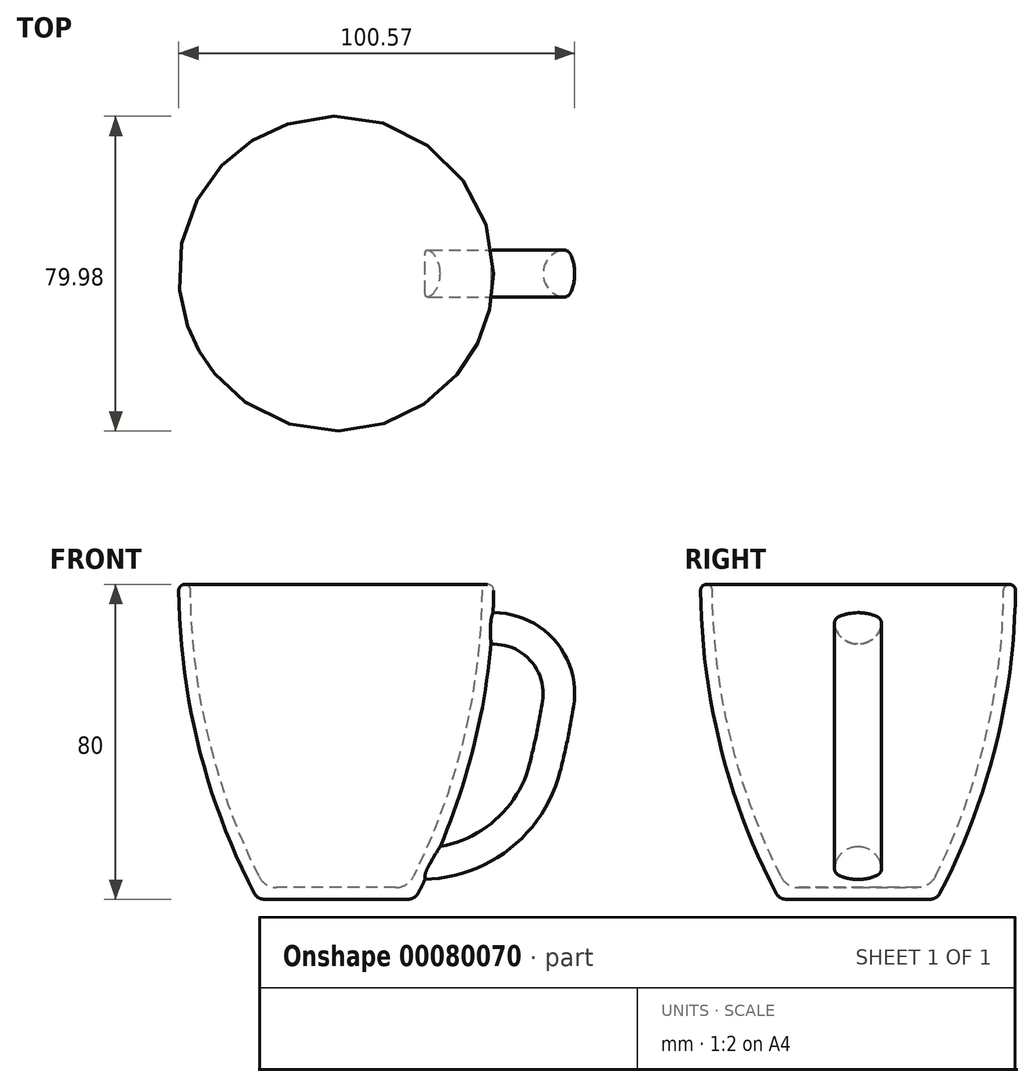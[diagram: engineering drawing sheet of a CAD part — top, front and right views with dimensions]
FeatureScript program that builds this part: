
annotation { "Feature Type Name" : "Feature", "Feature Type Description" : "" }
export const myFeature = defineFeature(function(context is Context, id is Id, definition is map)
    precondition{}
    {
        {
            var Q0;
            Q0=qCreatedBy(makeId("Front.planeOp"),FACE);
            var sketch = newSketch(context, id + "F0", { "sketchPlane" : qUnion([Q0])});
            skLineSegment(sketch, "E0", {"start": v(0, 3) * mm, "end": v(0, 0) * mm});
            skLineSegment(sketch, "E1", {"start": v(0, 0) * mm, "end": v(20, 0) * mm});
            skArc(sketch, "E2", {"start": v(20, 0) * mm, "mid": v(34.92, 38.77) * mm, "end": v(40, 80) * mm});
            skArc(sketch, "E3.0", {"start": v(18.19, 3) * mm, "mid": v(32.23, 40.37) * mm, "end": v(37, 80) * mm});
            skLineSegment(sketch, "E3.1", {"start": v(0, 3) * mm, "end": v(18.19, 3) * mm});
            skLineSegment(sketch, "E4", {"start": v(37, 80) * mm, "end": v(40, 80) * mm});
            skLineSegment(sketch, "E5", {"start": v(40, 160) * mm, "end": v(40, 0) * mm, "construction": true});
            skLineSegment(sketch, "E6", {"start": v(37, 160) * mm, "end": v(37, 0) * mm, "construction": true});
            skSolve(sketch);
        }
        {
            var Q0;
            Q0=qSketchRegion(id+"F0",true);
            var Q1;
            Q1=sQuery(id+"F0.wireOp",EDGE,"E0");
            revolve(context, id + "F1", {"entities" : qUnion([Q0]), "axis" : qUnion([Q1]), "revolveType" : RevolveType.FULL});
        }
        {
            var Q0;
            Q0=sQuery(id+"F0.wireOp",EDGE,"E5");
            cPlane(context, id + "F2", {"entities" : qUnion([Q0]), "cplaneType" : CPlaneType.LINE_ANGLE, "offset" : 150 * mm, "angle" : 0 * degree, "width" : 150 * mm, "height" : 150 * mm});
        }
        {
            var Q0;
            Q0=qCreatedBy(id+"F2.planeOp",FACE);
            var sketch = newSketch(context, id + "F3", { "sketchPlane" : qUnion([Q0])});
            skPoint(sketch, "E7", {"position": v(0, 70) * mm});
            skArc(sketch, "E8", {"start": v(4.8, 71.83) * mm, "mid": v(0, 72.83) * mm, "end": v(-4.8, 71.83) * mm});
            skArc(sketch, "E9", {"start": v(4.8, 71.83) * mm, "mid": v(5.79, 70.9) * mm, "end": v(5.95, 69.54) * mm});
            skArc(sketch, "E10", {"start": v(-4.8, 71.83) * mm, "mid": v(-5.79, 70.9) * mm, "end": v(-5.95, 69.54) * mm});
            skArc(sketch, "E11", {"start": v(-5.95, 69.54) * mm, "mid": v(0, 64.83) * mm, "end": v(5.95, 69.54) * mm});
            skSolve(sketch);
        }
        {
            var Q0;
            Q0=qSketchRegion(id+"F3",true);
            extrude(context, id + "F4", {"entities" : qUnion([Q0]), "operationType" : NewBodyOperationType.ADD, "endBound" : BoundingType.UP_TO_NEXT, "depth" : 25 * mm});
        }
        {
            var Q0;
            Q0=qCreatedBy(makeId("Front.planeOp"),FACE);
            var sketch = newSketch(context, id + "F5", { "sketchPlane" : qUnion([Q0])});
            skArc(sketch, "E12", {"start": v(57.52, 49.4) * mm, "mid": v(53.52, 63.75) * mm, "end": v(40, 70) * mm});
            skLineSegment(sketch, "E13", {"start": v(42.52, 70) * mm, "end": v(37.48, 70) * mm, "construction": true});
            skArc(sketch, "E14", {"start": v(54.14, 33.16) * mm, "mid": v(56, 41.24) * mm, "end": v(57.52, 49.4) * mm});
            skArc(sketch, "E15", {"start": v(54.14, 33.16) * mm, "mid": v(43.14, 15.7) * mm, "end": v(24, 8) * mm});
            skLineSegment(sketch, "E16", {"start": v(-130, 80) * mm, "end": v(57.52, 49.4) * mm, "construction": true});
            skLineSegment(sketch, "E17", {"start": v(-130, 80) * mm, "end": v(54.14, 33.16) * mm, "construction": true});
            skSolve(sketch);
        }
        {
            var Q0;
            Q0=makeQuery(id+"F3.imprint","IMPRINT",FACE,{"disambiguationData":[TD([[makeQuery(id+"F3.imprint","IMPRINT",EDGE,{"derivedFrom":sQuery(id+"F3.wireOp",EDGE,"E8")}),1.0]])]});
            var Q1;
            Q1=sQuery(id+"F5.wireOp",EDGE,"E12");
            var Q2;
            Q2=sQuery(id+"F5.wireOp",EDGE,"E14");
            var Q3;
            Q3=sQuery(id+"F5.wireOp",EDGE,"E15");
            sweep(context, id + "F6", {"operationType" : NewBodyOperationType.ADD, "profiles" : qUnion([Q0]), "path" : qUnion([Q1, Q2, Q3])});
        }
        {
            var Q0;
            Q0=makeQuery(id+"F1.opRevolve","SWEPT_EDGE",EDGE,{"disambiguationData":[OSD([sQuery(id+"F0.wireOp",EDGE,"E3.0"),sQuery(id+"F0.wireOp",EDGE,"E4")])]});
            var Q1;
            Q1=makeQuery(id+"F1.opRevolve","SWEPT_EDGE",EDGE,{"disambiguationData":[OSD([sQuery(id+"F0.wireOp",EDGE,"E2"),sQuery(id+"F0.wireOp",EDGE,"E4")])]});
            fillet(context, id + "F7", {"entities" : qUnion([Q0, Q1]), "radius" : 1.5 * mm, "tangentPropagation" : true, "allowEdgeOverflow" : false});
        }
        {
            var Q0;
            Q0=makeQuery(id+"F1.opRevolve","SWEPT_EDGE",EDGE,{"disambiguationData":[OSD([sQuery(id+"F0.wireOp",EDGE,"E1"),sQuery(id+"F0.wireOp",EDGE,"E2")])]});
            fillet(context, id + "F8", {"entities" : qUnion([Q0]), "radius" : 3 * mm, "tangentPropagation" : true, "allowEdgeOverflow" : false});
        }
        {
            var Q0;
            Q0=makeQuery(id+"F1.opRevolve","SWEPT_EDGE",EDGE,{"disambiguationData":[OSD([sQuery(id+"F0.wireOp",EDGE,"E3.0"),sQuery(id+"F0.wireOp",EDGE,"E3.1")])]});
            fillet(context, id + "F9", {"entities" : qUnion([Q0]), "radius" : 5 * mm, "tangentPropagation" : true, "allowEdgeOverflow" : false});
        }
        {
            var Q0;
            Q0=makeQuery(id+"F6.opSweep","CAP_FACE",FACE,{"disambiguationData":[OSD([sQuery(id+"F3.wireOp",EDGE,"E8"),sQuery(id+"F3.wireOp",EDGE,"E9"),sQuery(id+"F3.wireOp",EDGE,"E10"),sQuery(id+"F3.wireOp",EDGE,"E11"),sQuery(id+"F5.wireOp",VERTEX,"E15.end")])],"isStart":false});
            var sketch = newSketch(context, id + "F10", { "sketchPlane" : qUnion([Q0])});
            skArc(sketch, "E18", {"start": v(5.95, 6.77) * mm, "mid": v(5.84, 7.17) * mm, "end": v(5.7, 7.57) * mm});
            skArc(sketch, "E19", {"start": v(4.8, 4.48) * mm, "mid": v(5.79, 5.41) * mm, "end": v(5.95, 6.77) * mm});
            skArc(sketch, "E20", {"start": v(-4.8, 4.48) * mm, "mid": v(0, 3.47) * mm, "end": v(4.8, 4.48) * mm});
            skArc(sketch, "E21", {"start": v(-5.95, 6.77) * mm, "mid": v(-5.79, 5.41) * mm, "end": v(-4.8, 4.48) * mm});
            skArc(sketch, "E22", {"start": v(-5.7, 7.57) * mm, "mid": v(-5.84, 7.17) * mm, "end": v(-5.95, 6.77) * mm});
            skLineSegment(sketch, "E23", {"start": v(5.7, 7.57) * mm, "end": v(-5.7, 7.57) * mm});
            skSolve(sketch);
        }
        {
            var Q0;
            Q0=qSketchRegion(id+"F10",true);
            var Q1;
            Q1=makeQuery(id+"F1.opRevolve","SWEPT_FACE",FACE,{"disambiguationData":[OSD([sQuery(id+"F0.wireOp",EDGE,"E3.0")])]});
            extrude(context, id + "F11", {"entities" : qUnion([Q0]), "operationType" : NewBodyOperationType.ADD, "endBound" : BoundingType.UP_TO_SURFACE, "endBoundEntityFace" : qUnion([Q1]), "depth" : 25 * mm});
        }
    });
